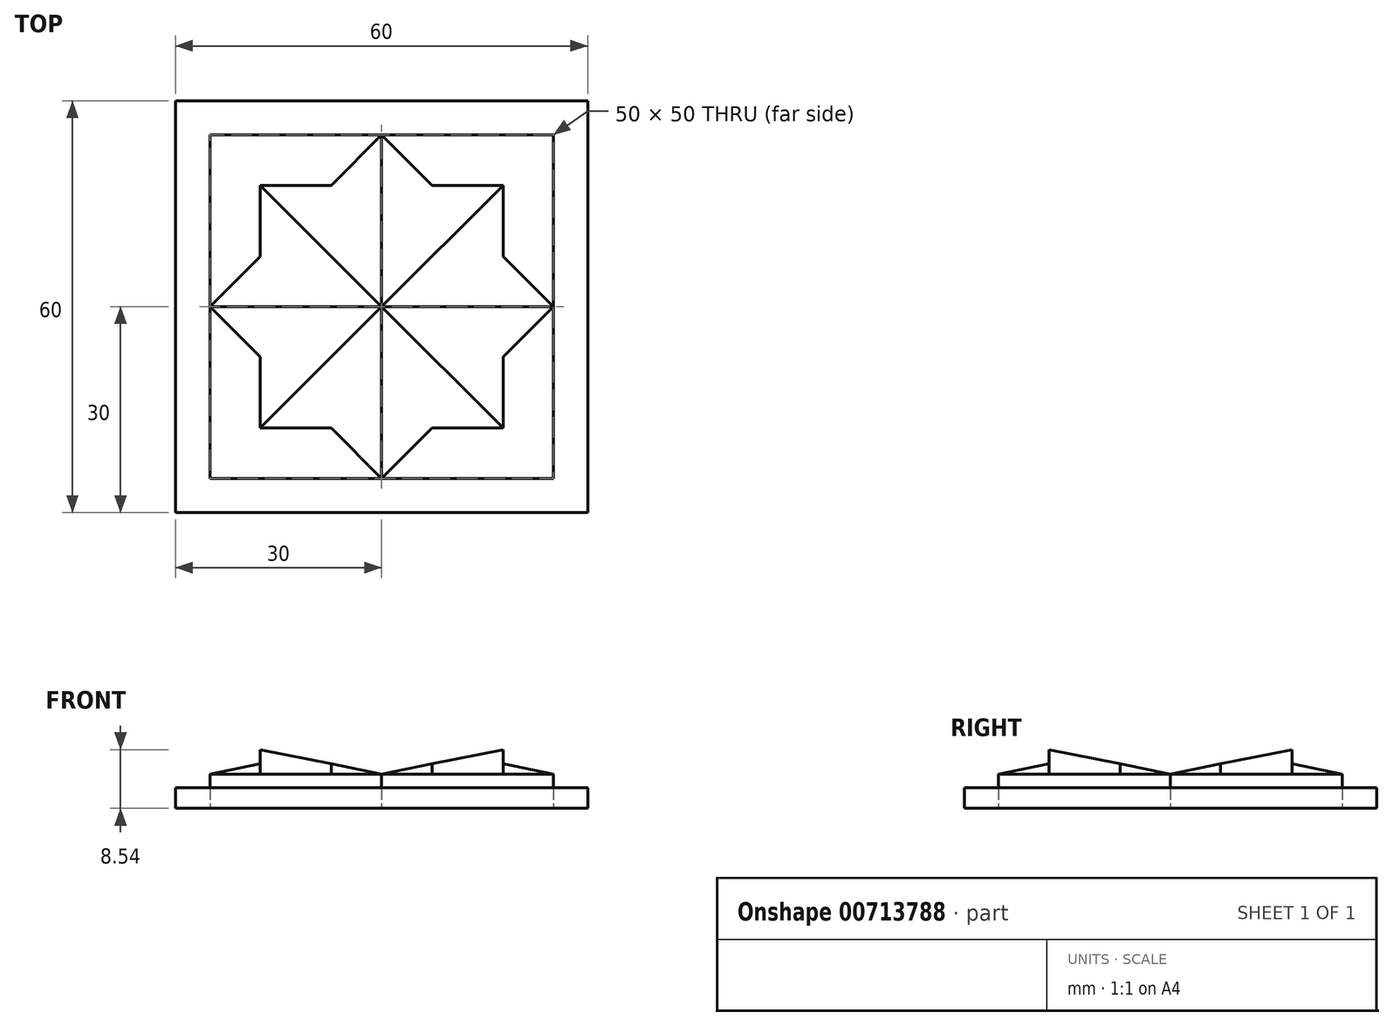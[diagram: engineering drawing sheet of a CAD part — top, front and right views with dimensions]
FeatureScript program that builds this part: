
annotation { "Feature Type Name" : "Feature", "Feature Type Description" : "" }
export const myFeature = defineFeature(function(context is Context, id is Id, definition is map)
    precondition{}
    {
        {
            var Q0;
            Q0=qCreatedBy(makeId("Top.planeOp"),FACE);
            var sketch = newSketch(context, id + "F0", { "sketchPlane" : qUnion([Q0])});
            skLineSegment(sketch, "E0.bottom", {"start": v(0, 0) * mm, "end": v(-25, 0) * mm});
            skLineSegment(sketch, "E0.top", {"start": v(0, 25) * mm, "end": v(-25, 25) * mm});
            skLineSegment(sketch, "E0.left", {"start": v(0, 0) * mm, "end": v(0, 25) * mm});
            skLineSegment(sketch, "E0.right", {"start": v(-25, 0) * mm, "end": v(-25, 25) * mm});
            skLineSegment(sketch, "E1", {"start": v(0, 0) * mm, "end": v(-25, 25) * mm});
            skSolve(sketch);
        }
        {
            var Q0;
            Q0=makeQuery(id+"F0.imprint","IMPRINT",FACE,{"disambiguationData":[TD([[makeQuery(id+"F0.imprint","IMPRINT",EDGE,{"derivedFrom":sQuery(id+"F0.wireOp",EDGE,"E0.bottom")}),-1.0]])]});
            var Q1;
            Q1=makeQuery(id+"F0.imprint","IMPRINT",FACE,{"disambiguationData":[TD([[makeQuery(id+"F0.imprint","IMPRINT",EDGE,{"derivedFrom":sQuery(id+"F0.wireOp",EDGE,"E0.top")}),1.0]])]});
            extrude(context, id + "F1", {"entities" : qUnion([Q0, Q1]), "depth" : 10 * mm, "offsetDistance" : 25 * mm});
        }
        {
            var Q0;
            Q0=makeQuery(id+"F1.opExtrude","CAP_EDGE",EDGE,{"disambiguationData":[OSD([sQuery(id+"F0.wireOp",EDGE,"E0.bottom")])],"isStart":false});
            var Q1;
            Q1=makeQuery(id+"F1.opExtrude","CAP_EDGE",EDGE,{"disambiguationData":[OSD([sQuery(id+"F0.wireOp",EDGE,"E0.left")])],"isStart":false});
            chamfer(context, id + "F2", {"entities" : qUnion([Q0, Q1]), "chamferType" : ChamferType.TWO_OFFSETS, "width1" : 5 * mm, "oppositeDirection" : false, "width2" : 25 * mm, "tangentPropagation" : true});
        }
        {
            var Q0;
            Q0=qCreatedBy(makeId("Front.planeOp"),FACE);
            var sketch = newSketch(context, id + "F3", { "sketchPlane" : qUnion([Q0])});
            skLineSegment(sketch, "E2", {"start": v(0, 58.18) * mm, "end": v(0, -59.07) * mm, "construction": true});
            skSolve(sketch);
        }
        {
            var Q0;
            Q0=makeQuery(id+"F1.opExtrude","SWEPT_BODY",BODY,{"disambiguationData":[OSD([sQuery(id+"F0.wireOp",EDGE,"E0.bottom"),sQuery(id+"F0.wireOp",EDGE,"E0.top"),sQuery(id+"F0.wireOp",EDGE,"E0.left"),sQuery(id+"F0.wireOp",EDGE,"E0.right")])]});
            var Q1;
            Q1=sQuery(id+"F3.wireOp",EDGE,"E2");
            circularPattern(context, id + "F4", {"entities" : qUnion([Q0]), "axis" : qUnion([Q1]), "angle" : 360 * degree, "instanceCount" : 4, "equalSpace" : true});
        }
        {
            var Q0;
            Q0=makeQuery(id+"F4.opPattern","COPY",FACE,{"derivedFrom":makeQuery(id+"F1.opExtrude","CAP_FACE",FACE,{"disambiguationData":[OSD([sQuery(id+"F0.wireOp",EDGE,"E0.bottom"),sQuery(id+"F0.wireOp",EDGE,"E0.top"),sQuery(id+"F0.wireOp",EDGE,"E0.left"),sQuery(id+"F0.wireOp",EDGE,"E0.right")])],"isStart":true}),"instanceName":"3"});
            var sketch = newSketch(context, id + "F5", { "sketchPlane" : qUnion([Q0])});
            skLineSegment(sketch, "E3.bottom", {"start": v(30, -30) * mm, "end": v(-30, -30) * mm});
            skLineSegment(sketch, "E3.top", {"start": v(30, 30) * mm, "end": v(-30, 30) * mm});
            skLineSegment(sketch, "E3.left", {"start": v(30, -30) * mm, "end": v(30, 30) * mm});
            skLineSegment(sketch, "E3.right", {"start": v(-30, -30) * mm, "end": v(-30, 30) * mm});
            skPoint(sketch, "E3.middle", {"position": v(0, 0) * mm});
            skLineSegment(sketch, "E4.bottom", {"start": v(25, -25) * mm, "end": v(-25, -25) * mm});
            skLineSegment(sketch, "E4.top", {"start": v(25, 25) * mm, "end": v(-25, 25) * mm});
            skLineSegment(sketch, "E4.left", {"start": v(25, -25) * mm, "end": v(25, 25) * mm});
            skLineSegment(sketch, "E4.right", {"start": v(-25, -25) * mm, "end": v(-25, 25) * mm});
            skSolve(sketch);
        }
        {
            var Q0;
            Q0 = qSketchRegion(id + "F5", true);
            extrude(context, id + "F6", {"entities" : qUnion([Q0]), "oppositeDirection" : true, "depth" : 15 * mm, "offsetDistance" : 25 * mm});
        }
        {
            var Q0;
            Q0=makeQuery(id+"F6.opExtrude","CAP_FACE",FACE,{"disambiguationData":[OSD([sQuery(id+"F5.wireOp",EDGE,"E3.bottom"),sQuery(id+"F5.wireOp",EDGE,"E3.top"),sQuery(id+"F5.wireOp",EDGE,"E3.left"),sQuery(id+"F5.wireOp",EDGE,"E3.right"),sQuery(id+"F5.wireOp",EDGE,"E4.bottom"),sQuery(id+"F5.wireOp",EDGE,"E4.top"),sQuery(id+"F5.wireOp",EDGE,"E4.left"),sQuery(id+"F5.wireOp",EDGE,"E4.right")])],"isStart":false});
            var sketch = newSketch(context, id + "F7", { "sketchPlane" : qUnion([Q0])});
            skLineSegment(sketch, "E5.0", {"start": v(25, 25) * mm, "end": v(0, 0) * mm, "construction": true});
            skLineSegment(sketch, "E6.0", {"start": v(25, 0) * mm, "end": v(0, 0) * mm, "construction": true});
            skLineSegment(sketch, "E7.0", {"start": v(25, -25) * mm, "end": v(0, 0) * mm, "construction": true});
            skLineSegment(sketch, "E8.0", {"start": v(0, 0) * mm, "end": v(0, 25) * mm, "construction": true});
            skLineSegment(sketch, "E9.0", {"start": v(0, 0) * mm, "end": v(-25, 25) * mm, "construction": true});
            skLineSegment(sketch, "E10.0", {"start": v(0, 0) * mm, "end": v(-25, 0) * mm, "construction": true});
            skLineSegment(sketch, "E11.0", {"start": v(-25, -25) * mm, "end": v(0, 0) * mm, "construction": true});
            skLineSegment(sketch, "E12.0", {"start": v(0, -25) * mm, "end": v(0, 0) * mm, "construction": true});
            skLineSegment(sketch, "E13.0", {"start": v(25, 25) * mm, "end": v(-25, 25) * mm, "construction": true});
            skLineSegment(sketch, "E14.0", {"start": v(25, 25) * mm, "end": v(25, -25) * mm, "construction": true});
            skLineSegment(sketch, "E15.0", {"start": v(25, -25) * mm, "end": v(-25, -25) * mm, "construction": true});
            skLineSegment(sketch, "E16.0", {"start": v(-25, 25) * mm, "end": v(-25, -25) * mm, "construction": true});
            skLineSegment(sketch, "E17", {"start": v(0, 25) * mm, "end": v(-25, 0) * mm});
            skLineSegment(sketch, "E18", {"start": v(-25, 0) * mm, "end": v(0, -25) * mm});
            skLineSegment(sketch, "E19", {"start": v(0, 25) * mm, "end": v(25, 0) * mm});
            skLineSegment(sketch, "E20", {"start": v(25, 0) * mm, "end": v(0, -25) * mm});
            skLineSegment(sketch, "E21", {"start": v(-17.68, 17.68) * mm, "end": v(17.68, 17.68) * mm});
            skLineSegment(sketch, "E22", {"start": v(17.68, -17.68) * mm, "end": v(-17.68, -17.68) * mm});
            skLineSegment(sketch, "E23", {"start": v(-17.68, -17.68) * mm, "end": v(-17.68, 17.68) * mm});
            skLineSegment(sketch, "E24", {"start": v(17.68, 17.68) * mm, "end": v(17.68, -17.68) * mm});
            skSolve(sketch);
        }
        {
            var Q0;
            {var subQ0=sQuery(id+"F7.wireOp",EDGE,"E24");var subQ1=sQuery(id+"F7.wireOp",EDGE,"E21");var subQ2=makeQuery(id+"F7.imprint","INTERSECT",VERTEX,{"derivedFrom":[subQ1,subQ0]});Q0=makeQuery(id+"F7.imprint","IMPRINT",FACE,{"disambiguationData":[TD([[makeQuery(id+"F7.imprint","IMPRINT",EDGE,{"disambiguationData":[TD([[subQ2,1.0]])],"derivedFrom":subQ1}),1.0]])]});}
            var Q1;
            {var subQ0=sQuery(id+"F7.wireOp",EDGE,"E23");var subQ1=sQuery(id+"F7.wireOp",EDGE,"E21");var subQ2=makeQuery(id+"F7.imprint","INTERSECT",VERTEX,{"derivedFrom":[subQ1,subQ0]});Q1=makeQuery(id+"F7.imprint","IMPRINT",FACE,{"disambiguationData":[TD([[makeQuery(id+"F7.imprint","IMPRINT",EDGE,{"disambiguationData":[TD([[subQ2,-1.0]])],"derivedFrom":subQ1}),1.0]])]});}
            var Q2;
            {var subQ0=sQuery(id+"F7.wireOp",EDGE,"E23");var subQ1=sQuery(id+"F7.wireOp",EDGE,"E22");var subQ2=makeQuery(id+"F7.imprint","INTERSECT",VERTEX,{"derivedFrom":[subQ1,subQ0]});Q2=makeQuery(id+"F7.imprint","IMPRINT",FACE,{"disambiguationData":[TD([[makeQuery(id+"F7.imprint","IMPRINT",EDGE,{"disambiguationData":[TD([[subQ2,1.0]])],"derivedFrom":subQ1}),1.0]])]});}
            var Q3;
            {var subQ0=sQuery(id+"F7.wireOp",EDGE,"E24");var subQ1=sQuery(id+"F7.wireOp",EDGE,"E22");var subQ2=makeQuery(id+"F7.imprint","INTERSECT",VERTEX,{"derivedFrom":[subQ1,subQ0]});Q3=makeQuery(id+"F7.imprint","IMPRINT",FACE,{"disambiguationData":[TD([[makeQuery(id+"F7.imprint","IMPRINT",EDGE,{"disambiguationData":[TD([[subQ2,-1.0]])],"derivedFrom":subQ1}),1.0]])]});}
            extrude(context, id + "F8", {"entities" : qUnion([Q0, Q1, Q2, Q3]), "operationType" : NewBodyOperationType.REMOVE, "oppositeDirection" : true, "depth" : 10 * mm, "offsetDistance" : 25 * mm});
        }
        {
            var Q0;
            Q0=makeQuery(id+"F6.opExtrude","CAP_FACE",FACE,{"disambiguationData":[OSD([sQuery(id+"F5.wireOp",EDGE,"E3.bottom"),sQuery(id+"F5.wireOp",EDGE,"E3.top"),sQuery(id+"F5.wireOp",EDGE,"E3.left"),sQuery(id+"F5.wireOp",EDGE,"E3.right"),sQuery(id+"F5.wireOp",EDGE,"E4.bottom"),sQuery(id+"F5.wireOp",EDGE,"E4.top"),sQuery(id+"F5.wireOp",EDGE,"E4.left"),sQuery(id+"F5.wireOp",EDGE,"E4.right")])],"isStart":false});
            extrude(context, id + "F9", {"entities" : qUnion([Q0]), "operationType" : NewBodyOperationType.REMOVE, "oppositeDirection" : true, "depth" : 12 * mm, "offsetDistance" : 25 * mm});
        }
    });
